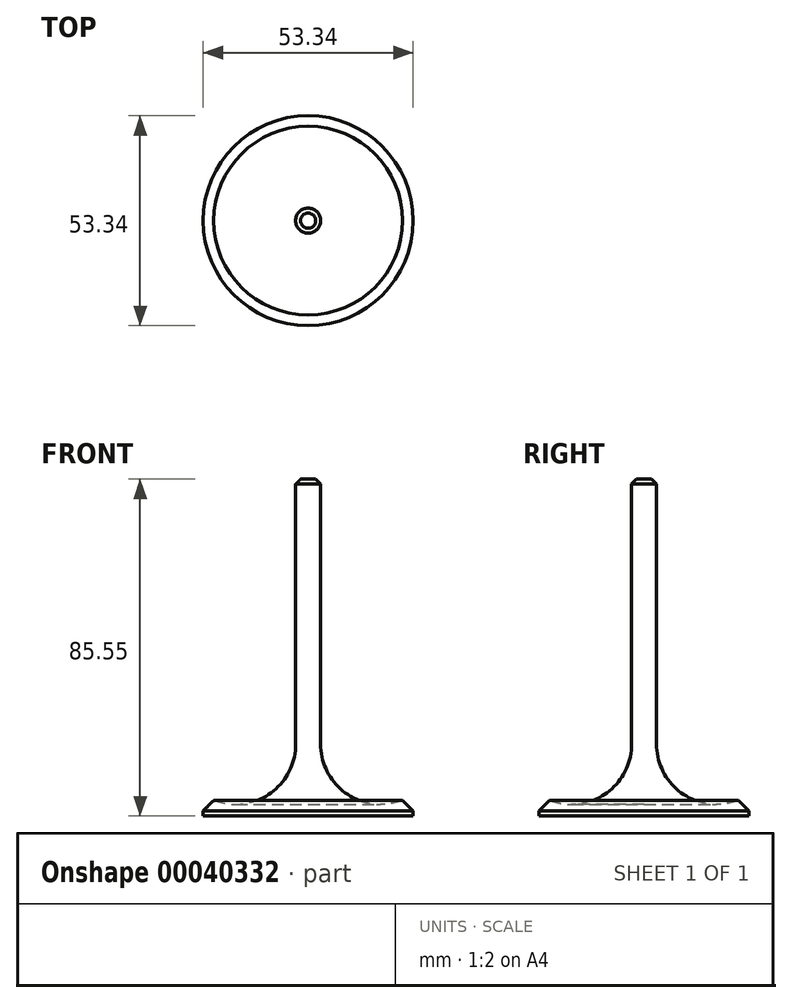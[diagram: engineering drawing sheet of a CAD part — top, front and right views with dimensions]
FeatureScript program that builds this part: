
annotation { "Feature Type Name" : "Feature", "Feature Type Description" : "" }
export const myFeature = defineFeature(function(context is Context, id is Id, definition is map)
    precondition{}
    {
        {
            var Q0;
            Q0=qCreatedBy(makeId("Front.planeOp"),FACE);
            var sketch = newSketch(context, id + "F0", { "sketchPlane" : qUnion([Q0])});
            skLineSegment(sketch, "E0", {"start": v(0, 0) * mm, "end": v(0, 85.55) * mm});
            skLineSegment(sketch, "E1", {"start": v(0, 85.55) * mm, "end": v(3.18, 85.55) * mm});
            skLineSegment(sketch, "E2", {"start": v(3.18, 85.55) * mm, "end": v(3.18, 18.17) * mm});
            skArc(sketch, "E3", {"start": v(3.18, 18.17) * mm, "mid": v(9.83, 5.58) * mm, "end": v(23.98, 3.96) * mm});
            skLineSegment(sketch, "E4", {"start": v(23.98, 3.96) * mm, "end": v(26.67, 1.27) * mm});
            skLineSegment(sketch, "E5", {"start": v(26.67, 1.27) * mm, "end": v(26.67, 0) * mm});
            skLineSegment(sketch, "E6", {"start": v(26.67, 0) * mm, "end": v(0, 0) * mm});
            skSolve(sketch);
        }
        {
            var Q0;
            Q0=makeQuery(id+"F0.imprint","IMPRINT",FACE,{"disambiguationData":[TD([[makeQuery(id+"F0.imprint","IMPRINT",EDGE,{"derivedFrom":sQuery(id+"F0.wireOp",EDGE,"E0")}),-1.0]])]});
            var Q1;
            Q1=sQuery(id+"F0.wireOp",EDGE,"E0");
            revolve(context, id + "F1", {"entities" : qUnion([Q0]), "axis" : qUnion([Q1]), "revolveType" : RevolveType.FULL});
        }
        {
            var Q0;
            Q0=makeQuery(id+"F1.opRevolve","SWEPT_EDGE",EDGE,{"disambiguationData":[OSD([sQuery(id+"F0.wireOp",EDGE,"E1"),sQuery(id+"F0.wireOp",EDGE,"E2")])]});
            chamfer(context, id + "F2", {"entities" : qUnion([Q0]), "width" : 1.25 * mm, "tangentPropagation" : true});
        }
    });
